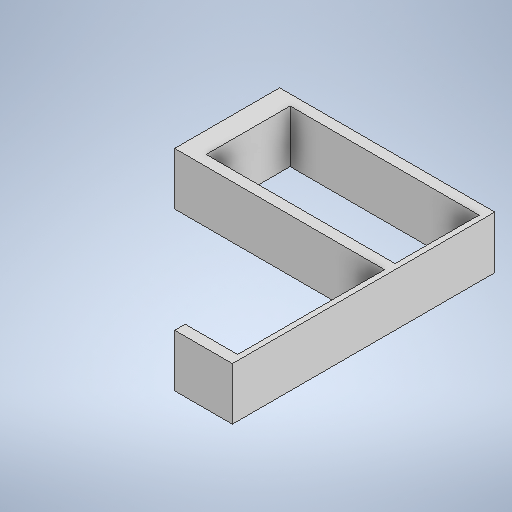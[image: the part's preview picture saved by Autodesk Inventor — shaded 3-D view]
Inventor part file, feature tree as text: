
AUTODESK INVENTOR PART (.ipt)
format: ipt  version: 2025.2 (Build 292293000, 293)  size: 242,688 bytes
history: native  units: mm
features: extrude x1, sketch x1
ambient origin geometry x8: Origin, YZ Plane, XZ Plane, XY Plane, X Axis, Y Axis, Z Axis, Center Point
bodies: Solid1 (feature_tree)
feature tree (2):
  extrude  "Extrusion1"  Depth=250.0mm
  sketch  "Sketch1"  dims[d0=5.0mm d1=250.0mm d2=50.0mm d3=10.0mm d4=150.0mm d5=200.0mm d6=10.0mm d7=20.0mm d8=100.0mm d9=10.0mm d10=10.0mm d11=50.0mm d12=0.0mm]
